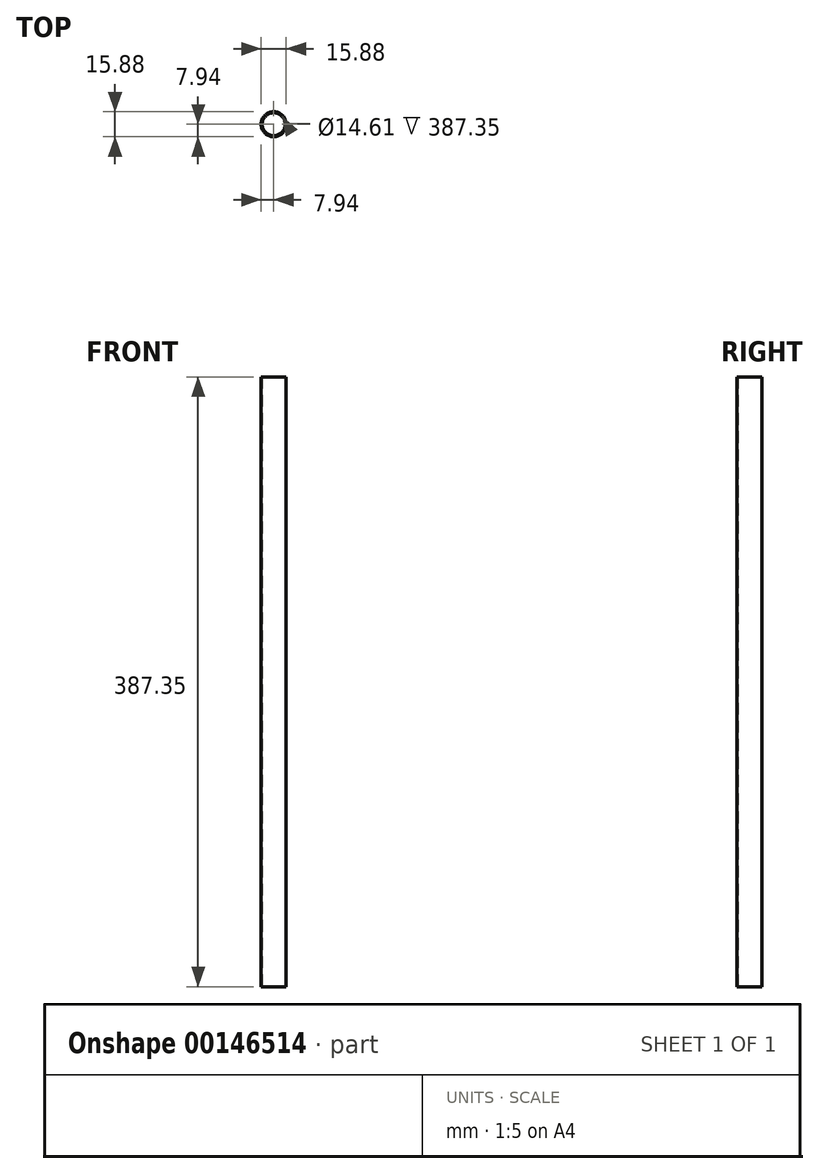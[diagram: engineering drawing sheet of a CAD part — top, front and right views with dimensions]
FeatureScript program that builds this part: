
annotation { "Feature Type Name" : "Feature", "Feature Type Description" : "" }
export const myFeature = defineFeature(function(context is Context, id is Id, definition is map)
    precondition{}
    {
        {
            var Q0;
            Q0=qCreatedBy(makeId("Top.planeOp"),FACE);
            var sketch = newSketch(context, id + "F0", { "sketchPlane" : qUnion([Q0])});
            skCircle(sketch, "E0", {"center": v(0, 0) * mm, "radius": 7.94 * mm});
            skCircle(sketch, "E1", {"center": v(0, 0) * mm, "radius": 7.3 * mm});
            skSolve(sketch);
        }
        {
            var Q0;
            Q0=makeQuery(id+"F0.imprint","IMPRINT",FACE,{"disambiguationData":[TD([[makeQuery(id+"F0.imprint","IMPRINT",EDGE,{"derivedFrom":sQuery(id+"F0.wireOp",EDGE,"E0")}),1.0]])]});
            var Q1;
            Q1=sQuery(id+"F0.wireOp",EDGE,"E1");
            extrude(context, id + "F1", {"entities" : qUnion([Q0]), "surfaceEntities" : qUnion([Q1]), "depth" : 387.35 * mm});
        }
    });
